# Revit family: Chair-Hussey-Quattro-Classic-2D
name_source: partatom
category: Furniture
units: mm (PartAtom-declared; Revit-internal decimal feet)

## family parameters
Always vertical = Yes
Classification Number = 23.40.50.11.11.11
Cut with Voids When Loaded = No
Enable Cutting in Views = No
Render Appearance Source = Family Geometry
Room Calculation Point = No
Shared = No
Work Plane-Based = No

## types (1)
- Chair-Hussey-Quattro-Classic-2D
    Assembly Code = E2010500
    BIM Version = v3.1
    BIM Version Available (Earliest) = 2017
    CSI MasterFormat = 12 61 00
    Default Elevation = 0"
    Description = Quattro Collection
    Designer Guide = Refer to Product Selector Worksheet for all Options
    Finish Options Website Link = http://204.239.146.105
    Manufacturer = Hussey Seating Company
    Model = Quattro Collection
    Product Brochure PDF = http://www.hscedocs.com
    Product Page URL = http://www.husseyseating.com
    Product Selector Worksheet Link = http://www.husseyseating.com
    Quattro Literature Downloads = http://www.husseyseating.com
    Seat Back Angle = 21.00°
    Seat Back Angle Note = 15°, 18° or 21°
    Seat Width Note = 19'', 20'', 21'', 22'', 23'', or 24''
    Series = Classic
    URL = http://www.husseyseating.com

## geometry (parser evidence)
native form markers: Sweep x4
no freeform markers — native parametric forms only
